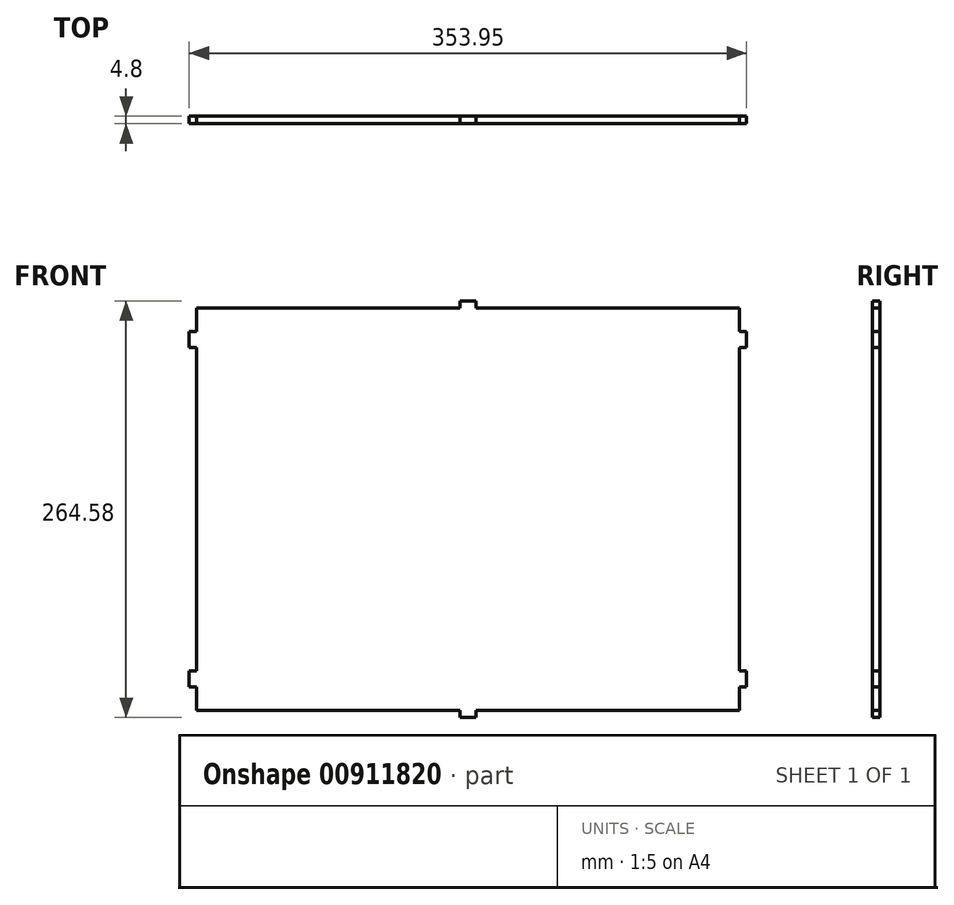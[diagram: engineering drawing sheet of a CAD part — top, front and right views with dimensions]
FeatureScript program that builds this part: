
annotation { "Feature Type Name" : "Feature", "Feature Type Description" : "" }
export const myFeature = defineFeature(function(context is Context, id is Id, definition is map)
    precondition{}
    {
        {
            var Q0;
            Q0=qCreatedBy(makeId("Front.planeOp"),FACE);
            var sketch = newSketch(context, id + "F0", { "sketchPlane" : qUnion([Q0])});
            skLineSegment(sketch, "E0", {"start": v(0, 0) * mm, "end": v(-344.95, 0) * mm});
            skLineSegment(sketch, "E1", {"start": v(0, 0) * mm, "end": v(0, 15) * mm});
            skLineSegment(sketch, "E2", {"start": v(0, 255.58) * mm, "end": v(-344.95, 255.58) * mm});
            skLineSegment(sketch, "E3", {"start": v(-344.95, 255.58) * mm, "end": v(-344.95, 240.58) * mm});
            skLineSegment(sketch, "E4", {"start": v(0, 255.58) * mm, "end": v(0, 240.58) * mm});
            skLineSegment(sketch, "E5", {"start": v(0, 240.58) * mm, "end": v(4.5, 240.58) * mm});
            skLineSegment(sketch, "E6", {"start": v(4.5, 240.58) * mm, "end": v(4.5, 230.58) * mm});
            skLineSegment(sketch, "E7", {"start": v(4.5, 230.58) * mm, "end": v(0, 230.58) * mm});
            skLineSegment(sketch, "E8.MirrorCS", {"start": v(4.5, 25) * mm, "end": v(0, 25) * mm});
            skLineSegment(sketch, "E9.MirrorCS", {"start": v(0, 15) * mm, "end": v(4.5, 15) * mm});
            skLineSegment(sketch, "E10.MirrorCS", {"start": v(-344.95, 240.58) * mm, "end": v(-349.45, 240.58) * mm});
            skLineSegment(sketch, "E11.MirrorCS", {"start": v(-349.45, 230.58) * mm, "end": v(-344.95, 230.58) * mm});
            skLineSegment(sketch, "E12.MirrorCS", {"start": v(-349.45, 25) * mm, "end": v(-344.95, 25) * mm});
            skLineSegment(sketch, "E13.MirrorCS", {"start": v(-344.95, 15) * mm, "end": v(-349.75, 15) * mm});
            skPoint(sketch, "E14.orphan", {"position": v(-172.48, 255.58) * mm});
            skPoint(sketch, "E15.orphan", {"position": v(0, 127.8) * mm});
            skPoint(sketch, "E16.end.orphan", {"position": v(-172.48, 0) * mm});
            skPoint(sketch, "E17.start.orphan", {"position": v(-344.95, 127.8) * mm});
            skLineSegment(sketch, "E18.trimOffspring", {"start": v(0, 25) * mm, "end": v(0, 230.58) * mm});
            skLineSegment(sketch, "E19.trimOffspring", {"start": v(-344.95, 15) * mm, "end": v(-344.95, 0) * mm});
            skLineSegment(sketch, "E20.trimOffspring", {"start": v(-344.95, 230.58) * mm, "end": v(-344.95, 25) * mm});
            skLineSegment(sketch, "E21.trimOffspring", {"start": v(0, 240.58) * mm, "end": v(0, 255.58) * mm});
            skLineSegment(sketch, "E22", {"start": v(-172.48, 0) * mm, "end": v(-172.48, -4.5) * mm});
            skLineSegment(sketch, "E23", {"start": v(-172.48, -4.5) * mm, "end": v(-177.48, -4.5) * mm});
            skLineSegment(sketch, "E24", {"start": v(-177.48, -4.5) * mm, "end": v(-177.48, 0) * mm});
            skLineSegment(sketch, "E25.MirrorCS", {"start": v(-172.48, -4.5) * mm, "end": v(-167.48, -4.5) * mm});
            skLineSegment(sketch, "E26.MirrorCS", {"start": v(-167.48, -4.5) * mm, "end": v(-167.48, 0) * mm});
            skLineSegment(sketch, "E27", {"start": v(0, 127.8) * mm, "end": v(-344.95, 127.8) * mm});
            skLineSegment(sketch, "E28.MirrorCS", {"start": v(-177.48, 260.08) * mm, "end": v(-177.48, 255.58) * mm});
            skLineSegment(sketch, "E29.MirrorCS", {"start": v(-172.48, 260.08) * mm, "end": v(-177.48, 260.08) * mm});
            skLineSegment(sketch, "E30.MirrorCS", {"start": v(-172.48, 260.08) * mm, "end": v(-167.48, 260.08) * mm});
            skLineSegment(sketch, "E31.MirrorCS", {"start": v(-167.48, 260.08) * mm, "end": v(-167.48, 255.58) * mm});
            skLineSegment(sketch, "E32", {"start": v(-349.45, 25) * mm, "end": v(-349.45, 15) * mm});
            skLineSegment(sketch, "E33", {"start": v(4.5, 25) * mm, "end": v(4.5, 15) * mm});
            skLineSegment(sketch, "E34", {"start": v(-349.45, 240.58) * mm, "end": v(-349.45, 230.58) * mm});
            skSolve(sketch);
        }
        {
            var Q0;
            Q0=makeQuery(id+"F0.imprint","IMPRINT",FACE,{"disambiguationData":[TD([[makeQuery(id+"F0.imprint","IMPRINT",EDGE,{"derivedFrom":sQuery(id+"F0.wireOp",EDGE,"E0")}),-1.0]])]});
            var Q1;
            {var subQ0=sQuery(id+"F0.wireOp",EDGE,"E22");Q1=makeQuery(id+"F0.imprint","IMPRINT",FACE,{"disambiguationData":[TD([[makeQuery(id+"F0.imprint","IMPRINT",EDGE,{"derivedFrom":subQ0}),1.0]])]});}
            var Q2;
            {var subQ0=sQuery(id+"F0.wireOp",EDGE,"E22");Q2=makeQuery(id+"F0.imprint","IMPRINT",FACE,{"disambiguationData":[TD([[makeQuery(id+"F0.imprint","IMPRINT",EDGE,{"derivedFrom":subQ0}),-1.0]])]});}
            var Q3;
            {var subQ7=sQuery(id+"F0.wireOp",EDGE,"E3");Q3=makeQuery(id+"F0.imprint","IMPRINT",FACE,{"disambiguationData":[TD([[makeQuery(id+"F0.imprint","IMPRINT",EDGE,{"derivedFrom":subQ7}),1.0]])]});}
            var Q4;
            {var subQ0=sQuery(id+"F0.wireOp",EDGE,"E28.MirrorCS");Q4=makeQuery(id+"F0.imprint","IMPRINT",FACE,{"disambiguationData":[TD([[makeQuery(id+"F0.imprint","IMPRINT",EDGE,{"derivedFrom":subQ0}),1.0]])]});}
            extrude(context, id + "F1", {"entities" : qUnion([Q0, Q1, Q2, Q3, Q4]), "depth" : 4.8 * mm, "offsetDistance" : 25 * mm});
        }
    });
